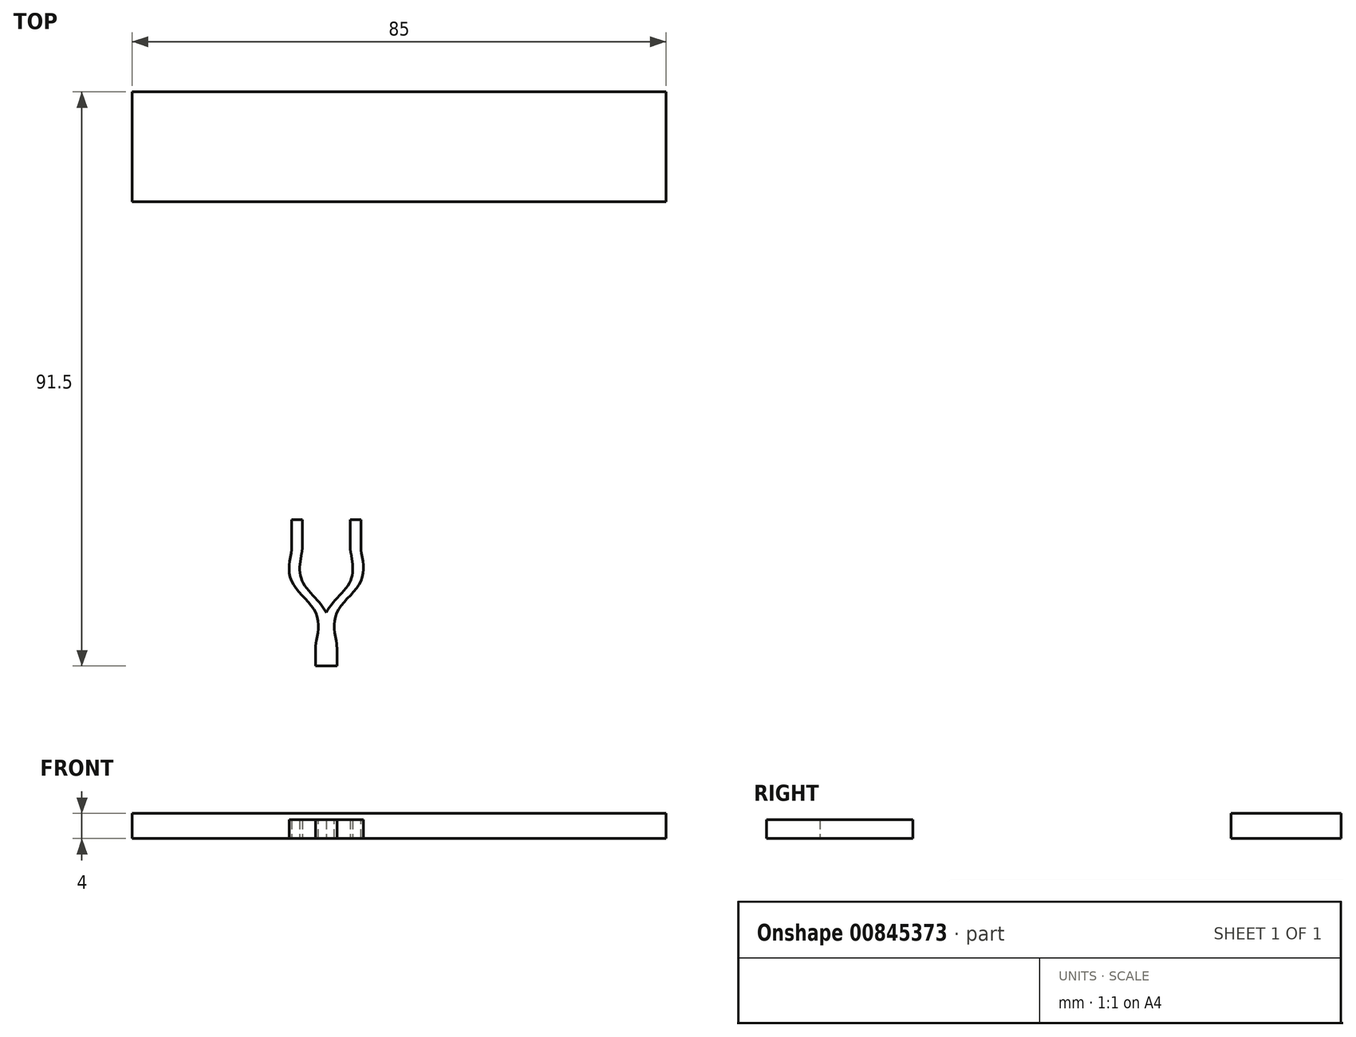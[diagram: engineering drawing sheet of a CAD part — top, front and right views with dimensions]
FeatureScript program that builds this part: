
annotation { "Feature Type Name" : "Feature", "Feature Type Description" : "" }
export const myFeature = defineFeature(function(context is Context, id is Id, definition is map)
    precondition{}
    {
        {
            var Q0;
            Q0=qCreatedBy(makeId("Top.planeOp"),FACE);
            var sketch = newSketch(context, id + "F0", { "sketchPlane" : qUnion([Q0])});
            skLineSegment(sketch, "E0.bottom", {"start": v(-64.97, 52.96) * mm, "end": v(20.03, 52.96) * mm});
            skLineSegment(sketch, "E0.top", {"start": v(-64.97, 35.46) * mm, "end": v(20.03, 35.46) * mm});
            skLineSegment(sketch, "E0.left", {"start": v(-64.97, 52.96) * mm, "end": v(-64.97, 35.46) * mm});
            skLineSegment(sketch, "E0.right", {"start": v(20.03, 52.96) * mm, "end": v(20.03, 35.46) * mm});
            skSolve(sketch);
        }
        {
            var Q0;
            Q0=qCreatedBy(makeId("Top.planeOp"),FACE);
            var sketch = newSketch(context, id + "F1", { "sketchPlane" : qUnion([Q0])});
            skLineSegment(sketch, "E1", {"start": v(-35.76, -38.54) * mm, "end": v(-32.38, -38.54) * mm});
            skLineSegment(sketch, "E2", {"start": v(-32.38, -38.54) * mm, "end": v(-32.38, -35.04) * mm});
            skLineSegment(sketch, "E3", {"start": v(-35.76, -38.54) * mm, "end": v(-35.76, -35.04) * mm});
            skPoint(sketch, "E4.startSnap0", {"position": v(-35.76, -35.04) * mm});
            skPoint(sketch, "E5", {"position": v(-34.07, -35.04) * mm});
            skLineSegment(sketch, "E6", {"start": v(-35.76, -35.04) * mm, "end": v(-32.38, -35.04) * mm});
            skLineSegment(sketch, "E7", {"start": v(-34.07, -35.04) * mm, "end": v(-34.07, -35.04) * mm});
            skLineSegment(sketch, "E8", {"start": v(-30.26, -20.04) * mm, "end": v(-28.57, -20.04) * mm});
            skLineSegment(sketch, "E9", {"start": v(-39.57, -20.04) * mm, "end": v(-37.88, -20.04) * mm});
            skLineSegment(sketch, "E10", {"start": v(-39.57, -20.04) * mm, "end": v(-38.32, -20.04) * mm});
            skFitSpline(sketch, "E11", {"points": [v(-35.76, -35.04) * mm, v(-35.76, -30.04) * mm, v(-39.57, -25.04) * mm, v(-39.57, -20.04) * mm], "startDerivative": vector(3.4, 16.15) * mm, "endDerivative": vector(3.4, 16.15) * mm});
            skFitSpline(sketch, "E12", {"points": [v(-34.07, -35.04) * mm, v(-34.07, -30.04) * mm, v(-37.88, -25.04) * mm, v(-37.88, -20.04) * mm], "startDerivative": vector(3.4, 16.15) * mm, "endDerivative": vector(3.4, 16.15) * mm});
            skFitSpline(sketch, "E13.MirrorCS", {"points": [v(-32.38, -35.04) * mm, v(-32.38, -30.04) * mm, v(-28.57, -25.04) * mm, v(-28.57, -20.04) * mm], "startDerivative": vector(-3.4, 16.15) * mm, "endDerivative": vector(-3.4, 16.15) * mm});
            skFitSpline(sketch, "E14.MirrorCS", {"points": [v(-34.07, -35.04) * mm, v(-34.07, -30.04) * mm, v(-30.26, -25.04) * mm, v(-30.26, -20.04) * mm], "startDerivative": vector(-3.4, 16.15) * mm, "endDerivative": vector(-3.4, 16.15) * mm});
            skLineSegment(sketch, "E15", {"start": v(-32.38, -35.04) * mm, "end": v(-32.38, -35.04) * mm});
            skLineSegment(sketch, "E16", {"start": v(-39.57, -20.04) * mm, "end": v(-39.57, -15.23) * mm});
            skLineSegment(sketch, "E17", {"start": v(-37.88, -20.04) * mm, "end": v(-37.88, -15.23) * mm});
            skLineSegment(sketch, "E18", {"start": v(-30.26, -20.04) * mm, "end": v(-30.26, -15.23) * mm});
            skLineSegment(sketch, "E19", {"start": v(-28.57, -20.04) * mm, "end": v(-28.57, -15.23) * mm});
            skLineSegment(sketch, "E20", {"start": v(-39.57, -15.23) * mm, "end": v(-37.88, -15.23) * mm});
            skLineSegment(sketch, "E21", {"start": v(-30.26, -15.23) * mm, "end": v(-28.57, -15.23) * mm});
            skSolve(sketch);
        }
        {
            var Q0;
            Q0 = qSketchRegion(id + "F0", true);
            extrude(context, id + "F2", {"entities" : qUnion([Q0]), "depth" : 4 * mm, "offsetDistance" : 25 * mm});
        }
        {
            var Q0;
            Q0 = qSketchRegion(id + "F1", true);
            extrude(context, id + "F3", {"entities" : qUnion([Q0]), "depth" : 3 * mm, "offsetDistance" : 25 * mm});
        }
        {
            var Q0;
            Q0=makeQuery(id+"F3.opExtrude","SWEPT_EDGE",EDGE,{"disambiguationData":[OSD([sQuery(id+"F1.wireOp",EDGE,"E8"),sQuery(id+"F1.wireOp",EDGE,"E14.MirrorCS"),sQuery(id+"F1.wireOp",EDGE,"E18")])]});
            var Q1;
            Q1=makeQuery(id+"F3.opExtrude","SWEPT_EDGE",EDGE,{"disambiguationData":[OSD([sQuery(id+"F1.wireOp",EDGE,"E9"),sQuery(id+"F1.wireOp",EDGE,"E12"),sQuery(id+"F1.wireOp",EDGE,"E17")])]});
            fillet(context, id + "F4", {"entities" : qUnion([Q0, Q1]), "radius" : 5 * mm, "tangentPropagation" : true, "allowEdgeOverflow" : false});
        }
        {
            var Q0;
            Q0=makeQuery(id+"F3.opExtrude","SWEPT_EDGE",EDGE,{"disambiguationData":[OSD([sQuery(id+"F1.wireOp",EDGE,"E10"),sQuery(id+"F1.wireOp",EDGE,"E11"),sQuery(id+"F1.wireOp",EDGE,"E16")])]});
            var Q1;
            Q1=makeQuery(id+"F3.opExtrude","SWEPT_EDGE",EDGE,{"disambiguationData":[OSD([sQuery(id+"F1.wireOp",EDGE,"E8"),sQuery(id+"F1.wireOp",EDGE,"E13.MirrorCS"),sQuery(id+"F1.wireOp",EDGE,"E19")])]});
            fillet(context, id + "F5", {"entities" : qUnion([Q0, Q1]), "radius" : 5 * mm, "tangentPropagation" : true, "allowEdgeOverflow" : false});
        }
        {
            var Q0;
            Q0=makeQuery(id+"F3.opExtrude","SWEPT_EDGE",EDGE,{"disambiguationData":[OSD([sQuery(id+"F1.wireOp",EDGE,"E13.MirrorCS"),sQuery(id+"F1.wireOp",EDGE,"E15")])]});
            var Q1;
            Q1=makeQuery(id+"F3.opExtrude","SWEPT_EDGE",EDGE,{"disambiguationData":[OSD([sQuery(id+"F1.wireOp",EDGE,"E3"),sQuery(id+"F1.wireOp",EDGE,"E6"),sQuery(id+"F1.wireOp",EDGE,"E11")])]});
            fillet(context, id + "F6", {"entities" : qUnion([Q0, Q1]), "radius" : 5 * mm, "tangentPropagation" : true, "allowEdgeOverflow" : false});
        }
    });
